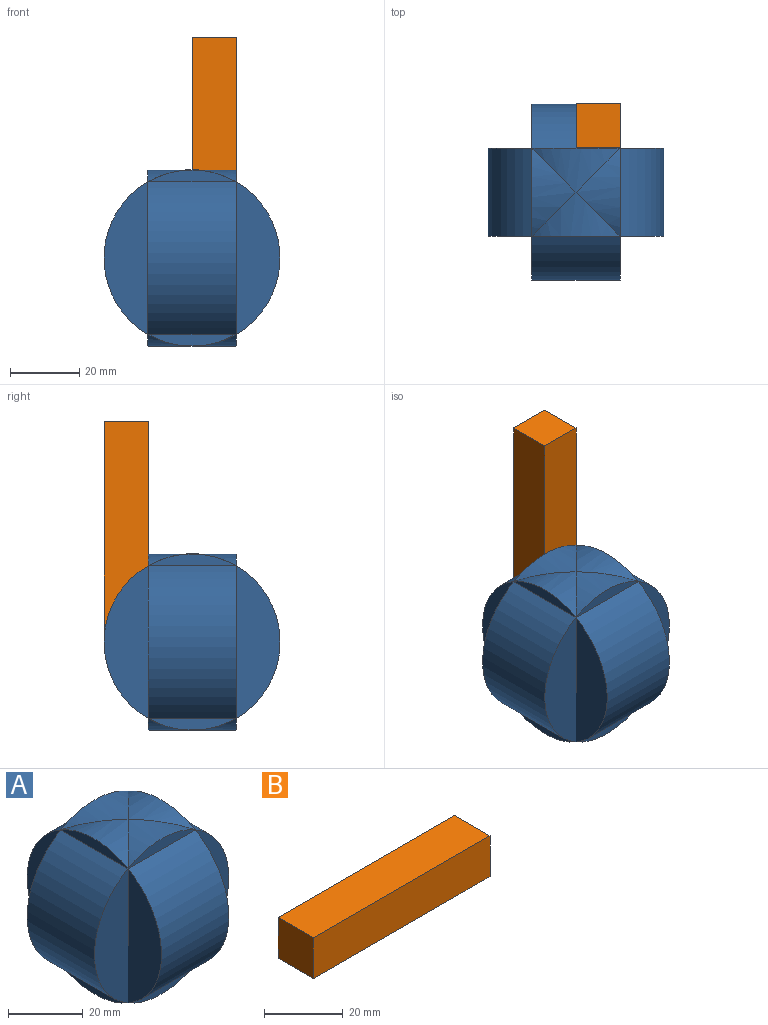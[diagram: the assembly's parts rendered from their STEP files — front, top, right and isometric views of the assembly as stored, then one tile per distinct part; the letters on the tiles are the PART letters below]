
ASSEMBLY  parts=2 mates=1
PART A: 28 faces, bbox 50.8x50.8x50.8 mm
  f0: cylinder r=25.4mm len=25.4mm, axis (-1,0,0), area 164.9mm2, adj f1,f8,f12
  f1: plane 25.4x3.4mm, normal (1,0,0), area 58.4mm2, adj f0,f4
  f2: plane 43.99x12.7mm, normal (0,-1,0), area 396.2mm2, adj f4,f19
  f3: plane 43.99x12.7mm, normal (0,1,0), area 396.2mm2, adj f4,f16
  f4: cylinder r=25.4mm len=43.99mm, axis (0,1,0), area 1351.2mm2, adj f1,f2,f3,f5
  f5: plane 25.4x3.4mm, normal (1,0,0), area 58.4mm2, adj f4,f6
  f6: cylinder r=25.4mm len=25.4mm, axis (-1,0,0), area 164.9mm2, adj f5,f10,f13
  f7: plane 25.4x3.4mm, normal (0,1,0), area 58.4mm2, adj f8,f17
  f8: cylinder r=25.4mm len=25.4mm, axis (0,1,0), area 164.9mm2, adj f0,f7,f24
  f9: plane 25.4x3.4mm, normal (0,1,0), area 58.4mm2, adj f10,f17
  f10: cylinder r=25.4mm len=25.4mm, axis (0,1,0), area 164.9mm2, adj f6,f9,f22
  f11: plane 25.4x3.4mm, normal (0,-1,0), area 58.4mm2, adj f12,f20
  f12: cylinder r=25.4mm len=25.4mm, axis (0,1,0), area 164.9mm2, adj f0,f11,f24
  f13: cylinder r=25.4mm len=25.4mm, axis (0,1,0), area 164.9mm2, adj f6,f14,f22
  f14: plane 25.4x3.4mm, normal (0,-1,0), area 58.4mm2, adj f13,f20
  f15: plane 43.99x12.7mm, normal (-1,0,0), area 396.2mm2, adj f17,f26
  f16: plane 43.99x12.7mm, normal (1,0,0), area 396.2mm2, adj f3,f17
  f17: cylinder r=25.4mm len=43.99mm, axis (-1,0,0), area 1351.2mm2, adj f7,f9,f15,f16
  f18: plane 43.99x12.7mm, normal (-1,0,0), area 396.2mm2, adj f20,f25
  f19: plane 43.99x12.7mm, normal (1,0,0), area 396.2mm2, adj f2,f20
  f20: cylinder r=25.4mm len=43.99mm, axis (-1,0,0), area 1351.2mm2, adj f11,f14,f18,f19
  f21: plane 25.4x3.4mm, normal (-1,0,0), area 58.4mm2, adj f22,f27
  f22: cylinder r=25.4mm len=25.4mm, axis (-1,0,0), area 164.9mm2, adj f10,f13,f21
  f23: plane 25.4x3.4mm, normal (-1,0,0), area 58.4mm2, adj f24,f27
  f24: cylinder r=25.4mm len=25.4mm, axis (-1,0,0), area 164.9mm2, adj f8,f12,f23
  f25: plane 43.99x12.7mm, normal (0,-1,0), area 396.2mm2, adj f18,f27
  f26: plane 43.99x12.7mm, normal (0,1,0), area 396.2mm2, adj f15,f27
  f27: cylinder r=25.4mm len=43.99mm, axis (0,1,0), area 1351.2mm2, adj f21,f23,f25,f26
PART B: 6 faces, bbox 63.5x12.7x12.7 mm
  f0: plane 63.5x12.7mm, normal (0,0,-1), area 806.5mm2, adj f1,f3,f4,f5
  f1: plane 12.7x12.7mm, normal (1,0,0), area 161.3mm2, adj f0,f2,f4,f5
  f2: plane 63.5x12.7mm, normal (0,0,1), area 806.5mm2, adj f1,f3,f4,f5
  f3: plane 12.7x12.7mm, normal (-1,0,0), area 161.3mm2, adj f0,f2,f4,f5
  f4: plane 63.5x12.7mm, normal (0,-1,0), area 806.5mm2, adj f0,f1,f2,f3
  f5: plane 63.5x12.7mm, normal (0,1,0), area 806.5mm2, adj f0,f1,f2,f3
PLACE A at identity
PLACE B rot(axis=(0.58,0.58,-0.58),120deg) t=(12.7,-24.56,28.44)mm
MATE ball B.f5 <-> A.f16  axis (1,0,0) through (12.7,12.7,0)mm
